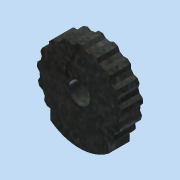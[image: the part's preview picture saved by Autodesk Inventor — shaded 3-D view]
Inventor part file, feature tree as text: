
AUTODESK INVENTOR PART (.ipt)
format: ipt  version: 2015 (Build 190159000, 159)  size: 178,176 bytes
history: native  units: in
note: dims shown in document units (in); Inventor stores cm internally (conversion verified against a paired STEP export)
features: extrude x3, sketch x2, other x1, pattern_circular x1
ambient origin geometry x8: Origin, YZ Plane, XZ Plane, XY Plane, X Axis, Y Axis, Z Axis, Center Point
bodies: Solid1 (feature_tree)
feature tree (7):
  other  "CaseRight.ipt"
  sketch  "Sketch2"  dims[d0=0.3937in d1=1.0in]
  extrude  "Extrusion1"  Depth=0.3937in
  extrude  "Extrusion2"  TaperAngle=15.0deg  [1 undecoded]
  pattern_circular  "Circular Pattern1"  [2 undecoded]
  extrude  "Extrusion3"  Depth=0.25in TaperAngle=0.0deg
  sketch  "Sketch3"  dims[d2=0.0312in d3=15.0deg d4=0.0412in d5=0.25in d6=0.0in d7=0.25in d8=0.0in d9=6.7492in d10=360.0deg d12=0.25in d13=75.0deg d14=1.125in d15=0.25in d16=0.0in]
note: 3 required parameter values undecoded (feature->parameter linkage not recoverable at this tier; creation-order binding heuristic only, values carry confidence <= 0.55)
